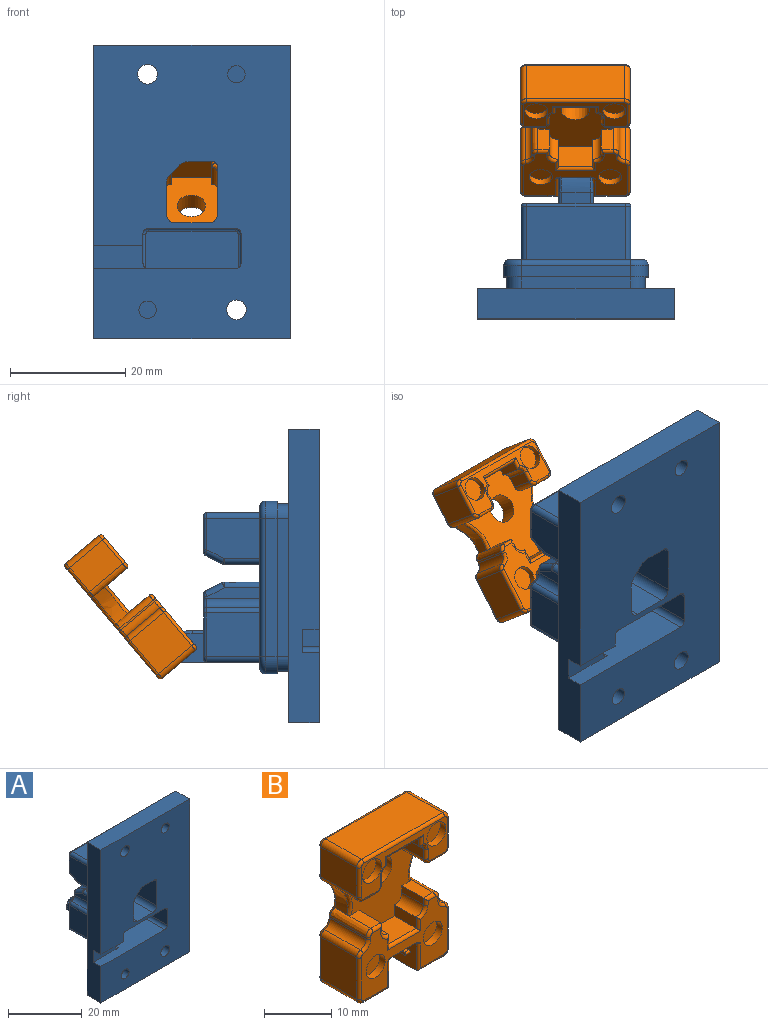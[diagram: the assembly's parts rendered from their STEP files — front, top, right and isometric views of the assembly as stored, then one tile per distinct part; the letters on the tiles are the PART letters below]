
ASSEMBLY  parts=2 mates=1
PART A: 202 faces, bbox 34.3x27.8x51.1 mm
  f0: plane 18.05x6.52mm, normal (0,1,0), area 53mm2, adj f152,f153,f154,f155,f156,f157,f158,f159
  f1: cylinder r=0.5mm len=5.5mm, axis (-1,0,0), area 4.3mm2, adj f30,f93,f148,f170
  f2: cylinder r=3mm len=6mm, axis (0,1,0), area 56.5mm2, adj f50,f112
  f3: cylinder r=1.5mm len=3mm, axis (0,-1,0), area 28.3mm2, adj f22,f111
  f4: cylinder r=1.7mm len=3.4mm, axis (0,1,0), area 24.6mm2, adj f22,f112
  f5: cylinder r=3mm len=6mm, axis (0,1,0), area 56.5mm2, adj f50,f100
  f6: cylinder r=1.7mm len=3.4mm, axis (0,1,0), area 24.6mm2, adj f22,f100
  f7: cylinder r=1.5mm len=3mm, axis (0,-1,0), area 28.3mm2, adj f22,f101
  f8: cylinder r=1.15mm len=4.55mm, axis (0,0,1), area 32.8mm2, adj f27,f86,f108
  f9: cylinder r=1.55mm len=3.1mm, axis (0,0,1), area 6.8mm2, adj f64,f110
  f10: cylinder r=1.55mm len=3.1mm, axis (0,0,1), area 6.8mm2, adj f64,f108
  f11: cylinder r=1.15mm len=4.55mm, axis (0,0,1), area 32.8mm2, adj f71,f72,f110
  f12: plane 2.54x2.54mm, normal (0,1,0), area 2.7mm2, adj f21,f32,f33,f126,f128,f129
  f13: plane 19.5x10.19mm, normal (-1,0,0), area 132.1mm2, adj f22,f24,f25,f26,f27,f28,f29,f31
  f14: plane 5.79x4.09mm, normal (0,0,-1), area 16.2mm2, adj f22,f126,f127,f128,f131
  f15: plane 50.8x5.3mm, normal (-1,0,0), area 257.6mm2, adj f22,f50,f55,f56,f57,f58,f125
  f16: cylinder r=1mm len=23.95mm, axis (0,0,-1), area 37.6mm2, adj f26,f44,f51,f114
  f17: cylinder r=1mm len=23.95mm, axis (0,0,1), area 37.6mm2, adj f26,f38,f40,f115
  f18: plane 9.2x6.97mm, normal (1,0,0), area 61.7mm2, adj f26,f36,f37,f122,f162
  f19: plane 9.2x6.97mm, normal (-1,0,0), area 61.7mm2, adj f26,f34,f35,f124,f154
  f20: plane 3.4x1.81mm, normal (0.71,0,-0.71), area 8.7mm2, adj f21,f22,f23,f127
  f21: plane 2.09x2.09mm, normal (0.5,0.71,-0.5), area 1.4mm2, adj f12,f20,f32,f126
  f22: plane 50.8x34mm, normal (0,-1,0), area 1453.5mm2, adj f3,f4,f6,f7,f13,f14,f15,f20
  f23: cylinder r=2mm len=3.4mm, axis (0,1,0), area 5.3mm2, adj f20,f22,f32,f33
  f24: cylinder r=1mm len=3.55mm, axis (0,-0.89,-0.45), area 5.3mm2, adj f13,f54,f88,f167
  f25: cylinder r=1mm len=6.1mm, axis (0,-1,0), area 9.6mm2, adj f13,f26,f87,f88
  f26: plane 28.01x23.06mm, normal (0,1,0), area 222.7mm2, adj f13,f16,f17,f18,f19,f25,f27,f33
  f27: plane 6.1x2.06mm, normal (0,0,1), area 8.9mm2, adj f8,f13,f26,f28,f86
  f28: cylinder r=1mm len=2.06mm, axis (-1,0,0), area 1mm2, adj f13,f27,f29,f89
  f29: plane 2.88x2.06mm, normal (0,0.45,0.89), area 6.6mm2, adj f13,f28,f90,f132,f133
  f30: plane 18.02x11.44mm, normal (0,1,0), area 115mm2, adj f1,f132,f133,f134,f135,f136,f137,f138
  f31: cylinder r=1.5mm len=19.5mm, axis (0,1,0), area 45.9mm2, adj f13,f22,f60,f135
  f32: cone r=2.4mm half-angle=45deg, axis (0,1,0), area 0.6mm2, adj f12,f21,f23,f33
  f33: plane 19.79x10.48mm, normal (1,0,0), area 121.7mm2, adj f12,f22,f23,f26,f32,f52,f61,f70
  f34: cylinder r=1mm len=3.55mm, axis (0,-0.89,-0.45), area 5.3mm2, adj f19,f53,f95,f152
  f35: cylinder r=1mm len=6.1mm, axis (0,-1,0), area 9.6mm2, adj f19,f26,f69,f95
  f36: cylinder r=1mm len=6.1mm, axis (0,1,0), area 9.6mm2, adj f18,f26,f87,f96
  f37: cylinder r=1mm len=3.55mm, axis (0,0.89,0.45), area 5.3mm2, adj f18,f54,f96,f164
  f38: torus R=2mm, axis (0,-1,0), area 6.5mm2, adj f17,f26,f41,f68
  f39: plane 29.95x25mm, normal (0,-1,0), area 50.5mm2, adj f40,f41,f42,f43,f44,f45,f46,f47
  f40: plane 23.95x2mm, normal (-1,0,0), area 47.9mm2, adj f17,f39,f41,f116
  f41: cylinder r=3mm len=3mm, axis (0,1,0), area 9.4mm2, adj f38,f39,f40,f42
  f42: plane 19x2mm, normal (0,0,-1), area 38mm2, adj f39,f41,f43,f68
  f43: cylinder r=3mm len=3mm, axis (0,-1,0), area 9.4mm2, adj f39,f42,f44,f51
  f44: plane 23.95x2mm, normal (1,0,0), area 47.9mm2, adj f16,f39,f43,f118
  f45: plane 24x2mm, normal (1,0,0), area 48mm2, adj f39,f46,f50,f119
  f46: cylinder r=2.5mm len=2.5mm, axis (0,-1,0), area 7.9mm2, adj f39,f45,f47,f50
  f47: plane 19x2mm, normal (0,0,-1), area 38mm2, adj f39,f46,f48,f50
  f48: cylinder r=2.5mm len=2.5mm, axis (0,-1,0), area 7.9mm2, adj f39,f47,f49,f50
  f49: plane 24x2mm, normal (-1,0,0), area 48mm2, adj f39,f48,f50,f121
  f50: plane 50.8x34mm, normal (0,1,0), area 980mm2, adj f2,f5,f15,f45,f46,f47,f48,f49
  f51: torus R=2mm, axis (0,-1,0), area 6.5mm2, adj f16,f26,f43,f68
  f52: cylinder r=1mm len=3.55mm, axis (0,0.89,0.45), area 5.3mm2, adj f33,f53,f97,f155
  f53: plane 3.01x2.87mm, normal (0,0.45,-0.89), area 9.7mm2, adj f34,f52,f98,f153
  f54: plane 3.01x2.87mm, normal (0,0.45,-0.89), area 9.7mm2, adj f24,f37,f99,f166
  f55: plane 34x5.3mm, normal (0,0,-1), area 180.2mm2, adj f15,f22,f50,f59
  f56: plane 24.5x10.3mm, normal (0,0,1), area 182mm2, adj f15,f22,f26,f57,f67,f79
  f57: plane 9.5x4mm, normal (0,-1,0), area 34.2mm2, adj f15,f56,f58,f62,f79
  f58: plane 8.5x2.9mm, normal (0,0,-1), area 24.6mm2, adj f15,f22,f57,f62
  f59: plane 50.8x5.3mm, normal (1,0,0), area 269.2mm2, adj f22,f50,f55,f125
  f60: plane 19.5x5.98mm, normal (0,0,1), area 116.6mm2, adj f22,f31,f61,f137
  f61: cylinder r=1.5mm len=19.5mm, axis (0,1,0), area 45.9mm2, adj f22,f33,f60,f139
  f62: plane 17.5x7.68mm, normal (1,0,0), area 96.8mm2, adj f22,f57,f58,f63,f77,f78,f79,f102
  f63: cylinder r=1mm len=17.5mm, axis (0,1,0), area 27.5mm2, adj f22,f62,f64,f103
  f64: plane 17.5x15mm, normal (0,0,-1), area 247.4mm2, adj f9,f10,f22,f63,f65,f104
  f65: cylinder r=1mm len=17.5mm, axis (0,1,0), area 27.5mm2, adj f22,f64,f66,f105
  f66: plane 17.5x7.68mm, normal (-1,0,0), area 105.5mm2, adj f22,f65,f67,f80,f81,f106
  f67: cylinder r=1mm len=10.8mm, axis (0,1,0), area 16.4mm2, adj f22,f26,f56,f66,f80
  f68: cylinder r=1mm len=19mm, axis (-1,0,0), area 29.8mm2, adj f26,f38,f42,f51
  f69: plane 6.1x3.01mm, normal (0,0,-1), area 18.4mm2, adj f26,f35,f70,f98
  f70: cylinder r=1mm len=6.1mm, axis (0,1,0), area 9.6mm2, adj f26,f33,f69,f97
  f71: plane 6.1x2.06mm, normal (0,0,1), area 8.9mm2, adj f11,f26,f33,f72,f94
  f72: cylinder r=1mm len=6.1mm, axis (0,-1,0), area 9.2mm2, adj f11,f26,f71,f73,f107
  f73: plane 9.2x1.91mm, normal (-1,0,0), area 15.2mm2, adj f26,f72,f74,f91,f147
  f74: cylinder r=1.5mm len=9.2mm, axis (0,1,0), area 18.6mm2, adj f26,f73,f75,f149
  f75: cylinder r=1mm len=9.2mm, axis (0,1,0), area 12.4mm2, adj f26,f74,f76,f151
  f76: plane 9.2x7.58mm, normal (-1,0,0), area 69.7mm2, adj f26,f75,f77,f150
  f77: cylinder r=1mm len=9.2mm, axis (0,1,0), area 14.6mm2, adj f26,f62,f76,f78,f93,f148
  f78: cylinder r=0.5mm len=2.68mm, axis (0,0,-1), area 1.7mm2, adj f26,f62,f77,f79
  f79: cylinder r=1mm len=7.9mm, axis (0,1,0), area 11.9mm2, adj f26,f56,f57,f62,f78
  f80: cylinder r=0.5mm len=2.68mm, axis (0,0,1), area 1.7mm2, adj f26,f66,f67,f81
  f81: cylinder r=1mm len=9.2mm, axis (0,-1,0), area 14.6mm2, adj f26,f66,f80,f82,f93,f144
  f82: plane 9.2x7.58mm, normal (1,0,0), area 69.7mm2, adj f26,f81,f83,f142
  f83: cylinder r=1mm len=9.2mm, axis (0,-1,0), area 12.4mm2, adj f26,f82,f84,f140
  f84: cylinder r=1.5mm len=9.2mm, axis (0,-1,0), area 18.6mm2, adj f26,f83,f85,f138
  f85: plane 9.2x1.91mm, normal (1,0,0), area 15.2mm2, adj f26,f84,f86,f90,f136
  f86: cylinder r=1mm len=6.1mm, axis (0,-1,0), area 9.2mm2, adj f8,f26,f27,f85,f89
  f87: plane 6.1x3.01mm, normal (0,0,-1), area 18.4mm2, adj f25,f26,f36,f99
  f88: sphere r=1mm, area 0.5mm2, adj f24,f25,f99
  f89: sphere r=1mm, area 0.4mm2, adj f28,f86,f90
  f90: cylinder r=1mm len=3.55mm, axis (0,-0.89,0.45), area 5.3mm2, adj f29,f85,f89,f134
  f91: cylinder r=1mm len=3.55mm, axis (0,0.89,-0.45), area 5.3mm2, adj f73,f92,f107,f145
  f92: plane 2.88x2.06mm, normal (0,0.45,0.89), area 6.6mm2, adj f33,f91,f94,f141,f143
  f93: plane 17.02x10.02mm, normal (0,0,-1), area 73.5mm2, adj f1,f77,f81,f102,f106,f109,f146,f168
  f94: cylinder r=1mm len=2.06mm, axis (-1,0,0), area 1mm2, adj f33,f71,f92,f107
  f95: sphere r=1mm, area 0.4mm2, adj f34,f35,f98
  f96: sphere r=1mm, area 0.5mm2, adj f36,f37,f99
  f97: sphere r=1mm, area 0.5mm2, adj f52,f70,f98
  f98: cylinder r=1mm len=3.01mm, axis (1,0,0), area 1.4mm2, adj f53,f69,f95,f97
  f99: cylinder r=1mm len=3.01mm, axis (1,0,0), area 1.4mm2, adj f54,f87,f88,f96
  f100: plane 6x6mm, normal (0,1,0), area 19.2mm2, adj f5,f6
  f101: plane 3x3mm, normal (0,-1,0), area 7.1mm2, adj f7
  f102: cylinder r=0.5mm len=7.68mm, axis (0,0,1), area 6mm2, adj f62,f93,f103,f109
  f103: torus R=0.5mm, axis (0,-1,0), area 1mm2, adj f63,f102,f104,f109
  f104: cylinder r=0.5mm len=15mm, axis (-1,0,0), area 11.8mm2, adj f64,f103,f105,f109
  f105: torus R=0.5mm, axis (0,-1,0), area 1mm2, adj f65,f104,f106,f109
  f106: cylinder r=0.5mm len=7.68mm, axis (0,0,1), area 6mm2, adj f66,f93,f105,f109
  f107: sphere r=1mm, area 0.5mm2, adj f72,f91,f94
  f108: plane 3.1x3.1mm, normal (0,0,-1), area 3.4mm2, adj f8,f10
  f109: plane 16.02x8.2mm, normal (0,-1,0), area 130.8mm2, adj f93,f102,f103,f104,f105,f106
  f110: plane 3.1x3.1mm, normal (0,0,-1), area 3.4mm2, adj f9,f11
  f111: plane 3x3mm, normal (0,-1,0), area 7.1mm2, adj f3
  f112: plane 6x6mm, normal (0,1,0), area 19.2mm2, adj f2,f4
  f113: cylinder r=1mm len=19mm, axis (-1,0,0), area 29.8mm2, adj f26,f114,f115,f117
  f114: torus R=2mm, axis (0,-1,0), area 6.5mm2, adj f16,f26,f113,f118
  f115: torus R=2mm, axis (0,-1,0), area 6.5mm2, adj f17,f26,f113,f116
  f116: cylinder r=3mm len=3mm, axis (0,-1,0), area 9.4mm2, adj f39,f40,f115,f117
  f117: plane 19x2mm, normal (0,0,1), area 38mm2, adj f39,f113,f116,f118
  f118: cylinder r=3mm len=3mm, axis (0,1,0), area 9.4mm2, adj f39,f44,f114,f117
  f119: cylinder r=2.5mm len=2.5mm, axis (0,-1,0), area 7.9mm2, adj f39,f45,f50,f120
  f120: plane 19x2mm, normal (0,0,1), area 38mm2, adj f39,f50,f119,f121
  f121: cylinder r=2.5mm len=2.5mm, axis (0,-1,0), area 7.9mm2, adj f39,f49,f50,f120
  f122: cylinder r=1mm len=9.2mm, axis (0,1,0), area 14.5mm2, adj f18,f26,f123,f160
  f123: plane 17x9.2mm, normal (0,0,1), area 156.4mm2, adj f26,f122,f124,f158
  f124: cylinder r=1mm len=9.2mm, axis (0,-1,0), area 14.5mm2, adj f19,f26,f123,f156
  f125: plane 34x5.3mm, normal (0,0,1), area 180.2mm2, adj f15,f22,f50,f59
  f126: cone r=2.4mm half-angle=45deg, axis (0,1,0), area 0.6mm2, adj f12,f14,f21,f127
  f127: cylinder r=2mm len=3.4mm, axis (0,1,0), area 5.3mm2, adj f14,f20,f22,f126
  f128: plane 15.77x6.98mm, normal (0,0.13,-0.99), area 111.1mm2, adj f12,f14,f129,f130,f161
  f129: cylinder r=1mm len=16.04mm, axis (0,-0.99,-0.13), area 24.9mm2, adj f12,f33,f128,f159
  f130: cylinder r=1mm len=15.97mm, axis (0,-0.99,-0.13), area 24.9mm2, adj f13,f128,f131,f163
  f131: cylinder r=1mm len=3.87mm, axis (0,-1,0), area 6mm2, adj f13,f14,f22,f130
  f132: cylinder r=0.5mm len=2.01mm, axis (-1,0,0), area 1mm2, adj f29,f30,f133,f134
  f133: cylinder r=0.5mm len=1.3mm, axis (0,0,-1), area 0.8mm2, adj f13,f29,f30,f132,f135
  f134: bspline ~1.01x1mm, area 0.8mm2, adj f30,f90,f132,f136
  f135: torus R=2mm, axis (0,1,0), area 2.1mm2, adj f30,f31,f133,f137
  f136: cylinder r=0.5mm len=0.5mm, axis (0,0,1), area 0.3mm2, adj f30,f85,f134,f138
  f137: cylinder r=0.5mm len=5.98mm, axis (-1,0,0), area 4.7mm2, adj f30,f60,f135,f139
  f138: torus R=2mm, axis (0,1,0), area 1.8mm2, adj f30,f84,f136,f140
  f139: torus R=2mm, axis (0,1,0), area 2.1mm2, adj f30,f61,f137,f141
  f140: torus R=0.5mm, axis (0,1,0), area 0.9mm2, adj f30,f83,f138,f142
  f141: cylinder r=0.5mm len=1.3mm, axis (0,0,1), area 0.8mm2, adj f30,f33,f92,f139,f143
  f142: cylinder r=0.5mm len=7.58mm, axis (0,0,1), area 6mm2, adj f30,f82,f140,f144
  f143: cylinder r=0.5mm len=2.01mm, axis (-1,0,0), area 1mm2, adj f30,f92,f141,f145
  f144: torus R=0.5mm, axis (0,1,0), area 1mm2, adj f30,f81,f142,f146
  f145: bspline ~1.01x1mm, area 0.8mm2, adj f30,f91,f143,f147
  f146: cylinder r=0.5mm len=5.5mm, axis (-1,0,0), area 4.3mm2, adj f30,f93,f144,f169
  f147: cylinder r=0.5mm len=0.5mm, axis (0,0,-1), area 0.3mm2, adj f30,f73,f145,f149
  f148: torus R=0.5mm, axis (0,1,0), area 1mm2, adj f1,f30,f77,f150
  f149: torus R=2mm, axis (0,1,0), area 1.8mm2, adj f30,f74,f147,f151
  f150: cylinder r=0.5mm len=7.58mm, axis (0,0,-1), area 6mm2, adj f30,f76,f148,f151
  f151: torus R=0.5mm, axis (0,1,0), area 0.9mm2, adj f30,f75,f149,f150
  f152: bspline ~1.01x1mm, area 0.8mm2, adj f0,f34,f153,f154
  f153: cylinder r=0.5mm len=3.01mm, axis (1,0,0), area 1.7mm2, adj f0,f53,f152,f155
  f154: cylinder r=0.5mm len=5.41mm, axis (0,0,-1), area 4.2mm2, adj f0,f19,f152,f156
  f155: bspline ~1.01x1mm, area 0.8mm2, adj f0,f52,f153,f157
  f156: torus R=0.5mm, axis (0,1,0), area 1mm2, adj f0,f124,f154,f158
  f157: cylinder r=0.5mm len=1.82mm, axis (0,0,1), area 1.4mm2, adj f0,f33,f155,f159
  f158: cylinder r=0.5mm len=17mm, axis (-1,0,0), area 13.4mm2, adj f0,f123,f156,f160
  f159: bspline ~1.51x1.5mm, area 1.4mm2, adj f0,f129,f157,f161
  f160: torus R=0.5mm, axis (0,1,0), area 1mm2, adj f0,f122,f158,f162
  f161: cylinder r=0.5mm len=6.98mm, axis (-1,0,0), area 5mm2, adj f0,f128,f159,f163
  f162: cylinder r=0.5mm len=5.41mm, axis (0,0,1), area 4.2mm2, adj f0,f18,f160,f164
  f163: bspline ~1.51x1.5mm, area 1.4mm2, adj f0,f130,f161,f165
  f164: bspline ~1.01x1mm, area 0.8mm2, adj f0,f37,f162,f166
  f165: cylinder r=0.5mm len=1.82mm, axis (0,0,-1), area 1.4mm2, adj f0,f13,f163,f167
  f166: cylinder r=0.5mm len=3.01mm, axis (1,0,0), area 1.7mm2, adj f0,f54,f164,f167
  f167: bspline ~1.01x1mm, area 0.8mm2, adj f0,f24,f165,f166
  f168: bspline ~6.6x5.5mm, area 44mm2, adj f93,f171,f172,f173,f179,f180,f181,f187
  f169: plane 7.5x5mm, normal (1,0,0), area 25.5mm2, adj f30,f93,f146,f172,f173,f174,f175,f176
  f170: plane 7.5x5mm, normal (-1,0,0), area 25.5mm2, adj f1,f30,f93,f180,f181,f182,f183,f184
  f171: plane 5x2mm, normal (0,0,1), area 10mm2, adj f30,f168,f189,f191
  f172: plane 1.2x1.08mm, normal (0,0,1), area 1.1mm2, adj f168,f169,f178,f179,f193
  f173: plane 1.12x0.99mm, normal (0,0,-1), area 0.8mm2, adj f168,f169,f174,f179,f188
  f174: cylinder r=1.1mm len=2.12mm, axis (1,0,0), area 2.8mm2, adj f169,f173,f175,f179
  f175: plane 2.41x1mm, normal (0,0,-1), area 2.4mm2, adj f169,f174,f176,f179
  f176: plane 1x0.6mm, normal (0,1,0), area 0.6mm2, adj f169,f175,f177,f179
  f177: plane 2.41x1mm, normal (0,0,1), area 2.4mm2, adj f169,f176,f178,f179
  f178: cylinder r=1.1mm len=2.12mm, axis (1,0,0), area 2.8mm2, adj f169,f172,f177,f179
  f179: plane 5.65x2.21mm, normal (1,0,0), area 5.8mm2, adj f168,f172,f173,f174,f175,f176,f177,f178
  f180: plane 1.12x0.99mm, normal (0,0,-1), area 0.8mm2, adj f168,f170,f186,f187,f190
  f181: plane 1.2x1.08mm, normal (0,0,1), area 1.1mm2, adj f168,f170,f182,f187,f192
  f182: cylinder r=1.1mm len=2.12mm, axis (-1,0,0), area 2.8mm2, adj f170,f181,f183,f187
  f183: plane 2.41x1mm, normal (0,0,1), area 2.4mm2, adj f170,f182,f184,f187
  f184: plane 1x0.6mm, normal (0,1,0), area 0.6mm2, adj f170,f183,f185,f187
  f185: plane 2.41x1mm, normal (0,0,-1), area 2.4mm2, adj f170,f184,f186,f187
  f186: cylinder r=1.1mm len=2.12mm, axis (-1,0,0), area 2.8mm2, adj f170,f180,f185,f187
  f187: plane 5.65x2.21mm, normal (-1,0,0), area 5.8mm2, adj f168,f180,f181,f182,f183,f184,f185,f186
  f188: bspline ~7.38x3.13mm, area 4.3mm2, adj f168,f169,f173,f189
  f189: cylinder r=0.5mm len=2mm, axis (0,1,0), area 1.6mm2, adj f30,f169,f171,f188
  f190: bspline ~7.38x3.13mm, area 4.3mm2, adj f168,f170,f180,f191
  f191: cylinder r=0.5mm len=2mm, axis (0,-1,0), area 1.6mm2, adj f30,f170,f171,f190
  f192: bspline ~3.29x1.08mm, area 2mm2, adj f93,f168,f170,f181
  f193: bspline ~3.29x1.08mm, area 2mm2, adj f93,f168,f169,f172
  f194: cylinder r=2mm len=4mm, axis (0,1,0), area 15.1mm2, adj f0,f195
  f195: plane 4x4mm, normal (0,1,0), area 12.6mm2, adj f194
  f196: cylinder r=2mm len=4mm, axis (0,1,0), area 15.1mm2, adj f0,f197
  f197: plane 4x4mm, normal (0,1,0), area 12.6mm2, adj f196
  f198: cylinder r=2mm len=4mm, axis (0,1,0), area 15.1mm2, adj f30,f199
  f199: plane 4x4mm, normal (0,1,0), area 12.6mm2, adj f198
  f200: cylinder r=2mm len=4mm, axis (0,1,0), area 15.1mm2, adj f30,f201
  f201: plane 4x4mm, normal (0,1,0), area 12.6mm2, adj f200
PART B: 142 faces, bbox 20.1x9.3x26.4 mm
  f0: plane 18x6.47mm, normal (0,-1,0), area 41mm2, adj f60,f61,f62,f63,f64,f65,f66,f67
  f1: plane 6.5x5mm, normal (-1,0,0), area 27.5mm2, adj f44,f55,f56,f57,f58,f78,f127,f128
  f2: plane 6.5x5mm, normal (1,0,0), area 27.5mm2, adj f44,f50,f51,f52,f53,f86,f130,f131
  f3: plane 18.19x11.61mm, normal (0,-1,0), area 96.2mm2, adj f48,f78,f79,f80,f81,f82,f83,f84
  f4: plane 4.5x1.5mm, normal (1,0,0), area 6.7mm2, adj f5,f21,f45,f75
  f5: extruded ~4.5x1.01mm, area 7.1mm2, adj f4,f6,f45,f77
  f6: plane 4.5x1.82mm, normal (1,0,0), area 8.2mm2, adj f5,f7,f45,f76
  f7: extruded ~4.5x1.06mm, area 7.3mm2, adj f6,f8,f45,f74
  f8: plane 5.14x3.15mm, normal (0,0,-1), area 13.6mm2, adj f7,f14,f45,f72,f125
  f9: plane 5.14x3.15mm, normal (0,0,-1), area 13.6mm2, adj f10,f20,f45,f63,f126
  f10: extruded ~4.5x1.06mm, area 7.3mm2, adj f9,f11,f45,f65
  f11: plane 4.5x1.82mm, normal (-1,0,0), area 8.2mm2, adj f10,f12,f45,f67
  f12: extruded ~4.5x1.01mm, area 7.1mm2, adj f11,f13,f45,f69
  f13: plane 4.5x1.5mm, normal (-1,0,0), area 6.7mm2, adj f12,f21,f45,f71
  f14: extruded ~7.5x1.06mm, area 12.1mm2, adj f8,f15,f47,f70,f112
  f15: plane 7.5x5.41mm, normal (-1,0,0), area 40.6mm2, adj f14,f16,f68,f114
  f16: cylinder r=1mm len=7.5mm, axis (0,-1,0), area 11.8mm2, adj f15,f17,f66,f116
  f17: plane 17x7.5mm, normal (0,0,1), area 127.5mm2, adj f16,f18,f64,f118
  f18: cylinder r=1mm len=7.5mm, axis (0,-1,0), area 11.8mm2, adj f17,f19,f62,f120
  f19: plane 7.5x5.41mm, normal (1,0,0), area 40.6mm2, adj f18,f20,f60,f122
  f20: extruded ~7.5x1.06mm, area 12.1mm2, adj f9,f19,f46,f61,f124
  f21: plane 6.98x4.5mm, normal (0,0,-1), area 31.4mm2, adj f4,f13,f45,f73
  f22: plane 24.95x18mm, normal (0,1,0), area 383.6mm2, adj f103,f104,f105,f106,f107,f108,f109,f110
  f23: cylinder r=1mm len=7.5mm, axis (0,-1,0), area 11.8mm2, adj f24,f44,f90,f107
  f24: plane 7.58x7.5mm, normal (-1,0,0), area 56.8mm2, adj f23,f25,f92,f105
  f25: cylinder r=1mm len=7.5mm, axis (0,-1,0), area 10.1mm2, adj f24,f26,f94,f103
  f26: cylinder r=1.5mm len=7.5mm, axis (0,-1,0), area 15.2mm2, adj f25,f27,f96,f104
  f27: plane 7.5x0.34mm, normal (-1,0,0), area 2.6mm2, adj f26,f28,f98,f106
  f28: extruded ~7.5x1.06mm, area 12.1mm2, adj f27,f29,f47,f100,f108
  f29: plane 5.03x2.09mm, normal (0,0,1), area 9.3mm2, adj f28,f30,f45,f102,f125
  f30: plane 4.5x1.24mm, normal (1,0,0), area 5.6mm2, adj f29,f31,f45,f101
  f31: cylinder r=1.5mm len=4.5mm, axis (0,-1,0), area 10.6mm2, adj f30,f32,f45,f99
  f32: plane 4.5x2mm, normal (1,0,0), area 9mm2, adj f31,f33,f45,f97
  f33: plane 5.98x4.5mm, normal (0,0,1), area 26.9mm2, adj f32,f34,f45,f95
  f34: plane 4.5x2mm, normal (-1,0,0), area 9mm2, adj f33,f35,f45,f93
  f35: cylinder r=1.5mm len=4.5mm, axis (0,-1,0), area 10.6mm2, adj f34,f36,f45,f91
  f36: plane 4.5x1.24mm, normal (-1,0,0), area 5.6mm2, adj f35,f37,f45,f89
  f37: plane 5.03x2.09mm, normal (0,0,1), area 9.3mm2, adj f36,f38,f45,f87,f126
  f38: extruded ~7.5x1.06mm, area 12.1mm2, adj f37,f39,f46,f85,f121
  f39: plane 7.5x0.34mm, normal (1,0,0), area 2.6mm2, adj f38,f40,f84,f119
  f40: cylinder r=1.5mm len=7.5mm, axis (0,-1,0), area 15.2mm2, adj f39,f41,f83,f117
  f41: cylinder r=1mm len=7.5mm, axis (0,-1,0), area 10.1mm2, adj f40,f42,f82,f115
  f42: plane 7.58x7.5mm, normal (1,0,0), area 56.8mm2, adj f41,f43,f81,f113
  f43: cylinder r=1mm len=7.5mm, axis (0,-1,0), area 11.8mm2, adj f42,f44,f80,f111
  f44: plane 17.02x7.52mm, normal (0,0,-1), area 85.6mm2, adj f1,f2,f23,f43,f49,f79,f88,f109
  f45: plane 16.2x15.79mm, normal (0,-1,0), area 140.9mm2, adj f4,f5,f6,f7,f8,f9,f10,f11
  f46: extruded ~6.07x2.5mm, area 16.5mm2, adj f20,f38,f123,f126
  f47: extruded ~6.07x2.5mm, area 16.5mm2, adj f14,f28,f110,f125
  f48: plane 5.27x2mm, normal (0,0,-1), area 10mm2, adj f3,f49,f128,f129,f131,f132
  f49: bspline ~6.6x5.5mm, area 44.6mm2, adj f44,f48,f127,f130
  f50: plane 1.5x0.9mm, normal (0,0,-1), area 1.3mm2, adj f2,f51,f53,f54
  f51: cylinder r=0.25mm len=0.9mm, axis (-1,0,0), area 0.7mm2, adj f2,f50,f52,f54
  f52: plane 1.5x0.9mm, normal (0,0,1), area 1.3mm2, adj f2,f51,f53,f54
  f53: cylinder r=0.25mm len=0.9mm, axis (-1,0,0), area 0.7mm2, adj f2,f50,f52,f54
  f54: plane 2x0.5mm, normal (1,0,0), area 0.9mm2, adj f50,f51,f52,f53
  f55: plane 1.5x0.9mm, normal (0,0,-1), area 1.3mm2, adj f1,f56,f58,f59
  f56: cylinder r=0.25mm len=0.9mm, axis (-1,0,0), area 0.7mm2, adj f1,f55,f57,f59
  f57: plane 1.5x0.9mm, normal (0,0,1), area 1.3mm2, adj f1,f56,f58,f59
  f58: cylinder r=0.25mm len=0.9mm, axis (-1,0,0), area 0.7mm2, adj f1,f55,f57,f59
  f59: plane 2x0.5mm, normal (-1,0,0), area 0.9mm2, adj f55,f56,f57,f58
  f60: cylinder r=0.5mm len=5.41mm, axis (0,0,-1), area 4.2mm2, adj f0,f19,f61,f62
  f61: bspline ~1.4x1.11mm, area 1mm2, adj f0,f20,f60,f63
  f62: torus R=0.5mm, axis (0,1,0), area 1mm2, adj f0,f18,f60,f64
  f63: cylinder r=0.5mm len=3.01mm, axis (-1,0,0), area 2.4mm2, adj f0,f9,f61,f65
  f64: cylinder r=0.5mm len=17mm, axis (1,0,0), area 13.4mm2, adj f0,f17,f62,f66
  f65: bspline ~1.4x1.27mm, area 1mm2, adj f0,f10,f63,f67
  f66: torus R=0.5mm, axis (0,1,0), area 1mm2, adj f0,f16,f64,f68
  f67: cylinder r=0.5mm len=1.82mm, axis (0,0,1), area 1.4mm2, adj f0,f11,f65,f69
  f68: cylinder r=0.5mm len=5.41mm, axis (0,0,1), area 4.2mm2, adj f0,f15,f66,f70
  f69: bspline ~1.83x1.68mm, area 1.3mm2, adj f0,f12,f67,f71
  f70: bspline ~1.4x1.27mm, area 1mm2, adj f0,f14,f68,f72
  f71: cylinder r=0.5mm len=2mm, axis (0,0,1), area 1.2mm2, adj f0,f13,f69,f73
  f72: cylinder r=0.5mm len=3.01mm, axis (-1,0,0), area 2.4mm2, adj f0,f8,f70,f74
  f73: cylinder r=0.5mm len=7.98mm, axis (-1,0,0), area 5.9mm2, adj f0,f21,f71,f75
  f74: bspline ~1.4x1.11mm, area 1mm2, adj f0,f7,f72,f76
  f75: cylinder r=0.5mm len=2mm, axis (0,0,-1), area 1.2mm2, adj f0,f4,f73,f77
  f76: cylinder r=0.5mm len=1.82mm, axis (0,0,-1), area 1.4mm2, adj f0,f6,f74,f77
  f77: bspline ~1.83x1.68mm, area 1.3mm2, adj f0,f5,f75,f76
  f78: cylinder r=0.5mm len=5mm, axis (0,0,1), area 3.7mm2, adj f1,f3,f79,f129
  f79: cylinder r=0.5mm len=5.5mm, axis (-1,0,0), area 4.1mm2, adj f3,f44,f78,f80
  f80: torus R=0.5mm, axis (0,1,0), area 1mm2, adj f3,f43,f79,f81
  f81: cylinder r=0.5mm len=7.58mm, axis (0,0,-1), area 6mm2, adj f3,f42,f80,f82
  f82: torus R=0.5mm, axis (0,1,0), area 0.9mm2, adj f3,f41,f81,f83
  f83: torus R=2mm, axis (0,1,0), area 1.8mm2, adj f3,f40,f82,f84
  f84: cylinder r=0.5mm len=0.5mm, axis (0,0,-1), area 0.3mm2, adj f3,f39,f83,f85
  f85: bspline ~1.27x1.18mm, area 1mm2, adj f3,f38,f84,f87
  f86: cylinder r=0.5mm len=5mm, axis (0,0,-1), area 3.7mm2, adj f2,f3,f88,f132
  f87: cylinder r=0.5mm len=2.06mm, axis (1,0,0), area 1.4mm2, adj f3,f37,f85,f89
  f88: cylinder r=0.5mm len=5.5mm, axis (-1,0,0), area 4.1mm2, adj f3,f44,f86,f90
  f89: cylinder r=0.5mm len=1.24mm, axis (0,0,1), area 0.8mm2, adj f3,f36,f87,f91
  f90: torus R=0.5mm, axis (0,1,0), area 1mm2, adj f3,f23,f88,f92
  f91: torus R=2mm, axis (0,1,0), area 1.9mm2, adj f3,f35,f89,f93
  f92: cylinder r=0.5mm len=7.58mm, axis (0,0,1), area 6mm2, adj f3,f24,f90,f94
  f93: cylinder r=0.5mm len=2.5mm, axis (0,0,1), area 1.6mm2, adj f3,f34,f91,f95
  f94: torus R=0.5mm, axis (0,1,0), area 0.9mm2, adj f3,f25,f92,f96
  f95: cylinder r=0.5mm len=6.98mm, axis (1,0,0), area 5.1mm2, adj f3,f33,f93,f97
  f96: torus R=2mm, axis (0,1,0), area 1.8mm2, adj f3,f26,f94,f98
  f97: cylinder r=0.5mm len=2.5mm, axis (0,0,-1), area 1.6mm2, adj f3,f32,f95,f99
  f98: cylinder r=0.5mm len=0.5mm, axis (0,0,1), area 0.3mm2, adj f3,f27,f96,f100
  f99: torus R=2mm, axis (0,1,0), area 1.9mm2, adj f3,f31,f97,f101
  f100: bspline ~1.4x1.11mm, area 1mm2, adj f3,f28,f98,f102
  f101: cylinder r=0.5mm len=1.24mm, axis (0,0,-1), area 0.8mm2, adj f3,f30,f99,f102
  f102: cylinder r=0.5mm len=2.06mm, axis (1,0,0), area 1.4mm2, adj f3,f29,f100,f101
  f103: torus R=0.5mm, axis (0,1,0), area 0.9mm2, adj f22,f25,f104,f105
  f104: torus R=2mm, axis (0,1,0), area 1.8mm2, adj f22,f26,f103,f106
  f105: cylinder r=0.5mm len=7.58mm, axis (0,0,-1), area 6mm2, adj f22,f24,f103,f107
  f106: cylinder r=0.5mm len=0.5mm, axis (0,0,-1), area 0.3mm2, adj f22,f27,f104,f108
  f107: torus R=0.5mm, axis (0,1,0), area 1mm2, adj f22,f23,f105,f109
  f108: bspline ~1.96x1.49mm, area 1.2mm2, adj f22,f28,f106,f110
  f109: cylinder r=0.5mm len=17mm, axis (1,0,0), area 13.4mm2, adj f22,f44,f107,f111
  f110: bspline ~15.77x4.37mm, area 5.6mm2, adj f22,f47,f108,f112
  f111: torus R=0.5mm, axis (0,1,0), area 1mm2, adj f22,f43,f109,f113
  f112: bspline ~1.49x1.46mm, area 1.2mm2, adj f14,f22,f110,f114
  f113: cylinder r=0.5mm len=7.58mm, axis (0,0,1), area 6mm2, adj f22,f42,f111,f115
  f114: cylinder r=0.5mm len=5.41mm, axis (0,0,-1), area 4.2mm2, adj f15,f22,f112,f116
  f115: torus R=0.5mm, axis (0,1,0), area 0.9mm2, adj f22,f41,f113,f117
  f116: torus R=0.5mm, axis (0,1,0), area 1mm2, adj f16,f22,f114,f118
  f117: torus R=2mm, axis (0,1,0), area 1.8mm2, adj f22,f40,f115,f119
  f118: cylinder r=0.5mm len=17mm, axis (-1,0,0), area 13.4mm2, adj f17,f22,f116,f120
  f119: cylinder r=0.5mm len=0.5mm, axis (0,0,1), area 0.3mm2, adj f22,f39,f117,f121
  f120: torus R=0.5mm, axis (0,1,0), area 1mm2, adj f18,f22,f118,f122
  f121: bspline ~1.96x1.49mm, area 1.2mm2, adj f22,f38,f119,f123
  f122: cylinder r=0.5mm len=5.41mm, axis (0,0,1), area 4.2mm2, adj f19,f22,f120,f124
  f123: bspline ~8x3.25mm, area 5.6mm2, adj f22,f46,f121,f124
  f124: bspline ~1.49x1.46mm, area 1.2mm2, adj f20,f22,f122,f123
  f125: bspline ~7x2.83mm, area 5.1mm2, adj f8,f29,f45,f47
  f126: bspline ~7x2.83mm, area 5.1mm2, adj f9,f37,f45,f46
  f127: bspline ~7.76x5.7mm, area 6.8mm2, adj f1,f44,f49,f128
  f128: cylinder r=0.5mm len=1.5mm, axis (0,-1,0), area 1.2mm2, adj f1,f48,f127,f129
  f129: torus R=1mm, axis (0,0,1), area 0.5mm2, adj f3,f48,f78,f128
  f130: bspline ~7.76x5.7mm, area 6.8mm2, adj f2,f44,f49,f131
  f131: cylinder r=0.5mm len=1.5mm, axis (0,1,0), area 1.2mm2, adj f2,f48,f130,f132
  f132: torus R=1mm, axis (0,0,1), area 0.5mm2, adj f3,f48,f86,f131
  f133: cone r=2.43mm half-angle=2.3deg, axis (0,1,0), area 55.1mm2, adj f22,f45
  f134: cylinder r=2mm len=4mm, axis (0,1,0), area 15.1mm2, adj f0,f135
  f135: plane 4x4mm, normal (0,-1,0), area 12.6mm2, adj f134
  f136: cylinder r=2mm len=4mm, axis (0,1,0), area 15.1mm2, adj f0,f137
  f137: plane 4x4mm, normal (0,-1,0), area 12.6mm2, adj f136
  f138: cylinder r=2mm len=4mm, axis (0,1,0), area 15.1mm2, adj f3,f139
  f139: plane 4x4mm, normal (0,-1,0), area 12.6mm2, adj f138
  f140: cylinder r=2mm len=4mm, axis (0,1,0), area 15.1mm2, adj f3,f141
  f141: plane 4x4mm, normal (0,-1,0), area 12.6mm2, adj f140
PLACE A t=(-6,-5.87,-3.72)mm
PLACE B rot(axis=(-1,0,0),40deg) t=(-6.1,9.52,8.05)mm
MATE revolute A.f182 <-> B.f59  axis (1,0,0) through (-4,19.09,-15.94)mm
